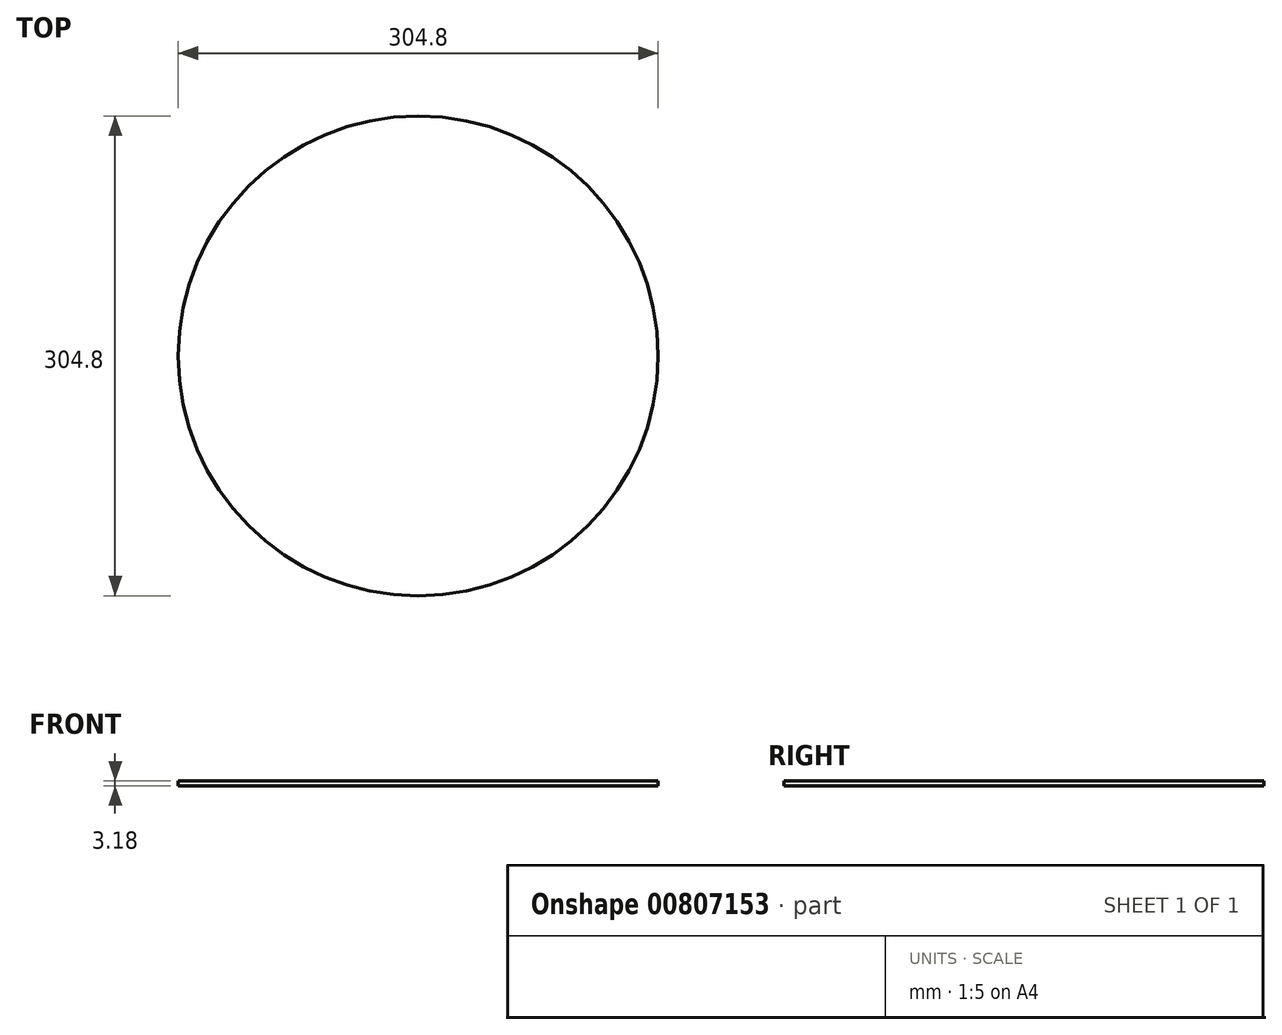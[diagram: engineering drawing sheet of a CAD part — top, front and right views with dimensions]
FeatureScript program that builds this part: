
annotation { "Feature Type Name" : "Feature", "Feature Type Description" : "" }
export const myFeature = defineFeature(function(context is Context, id is Id, definition is map)
    precondition{}
    {
        {
            var Q0;
            Q0=qCreatedBy(makeId("Top.planeOp"),FACE);
            var sketch = newSketch(context, id + "F0", { "sketchPlane" : qUnion([Q0])});
            skCircle(sketch, "E0", {"center": v(0, 0) * mm, "radius": 152.4 * mm});
            skSolve(sketch);
        }
        {
            var Q0;
            Q0=qSketchRegion(id+"F0",true);
            extrude(context, id + "F1", {"entities" : qUnion([Q0]), "depth" : 3.17 * mm, "offsetDistance" : 25.4 * mm});
        }
    });
